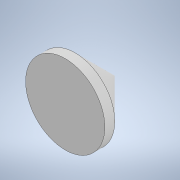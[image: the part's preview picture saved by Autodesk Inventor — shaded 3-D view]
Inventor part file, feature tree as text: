
AUTODESK INVENTOR PART (.ipt)
format: ipt  version: 2020 (Build 240168000, 168)  size: 103,936 bytes
history: native  units: in
note: dims shown in document units (in); Inventor stores cm internally (conversion verified against a paired STEP export)
features: revolve x1, sketch x1
ambient origin geometry x8: Origin, YZ Plane, XZ Plane, XY Plane, X Axis, Y Axis, Z Axis, Center Point
bodies: Body1 (feature_tree)
feature tree (2):
  revolve  "Revolution2"  [1 undecoded]
  sketch  "Sketch4"  dims[d7=3.1496in d8=3.937in d10=90.0deg d12=3.1496in]
note: 1 required parameter value undecoded (feature->parameter linkage not recoverable at this tier; creation-order binding heuristic only, values carry confidence <= 0.55)
